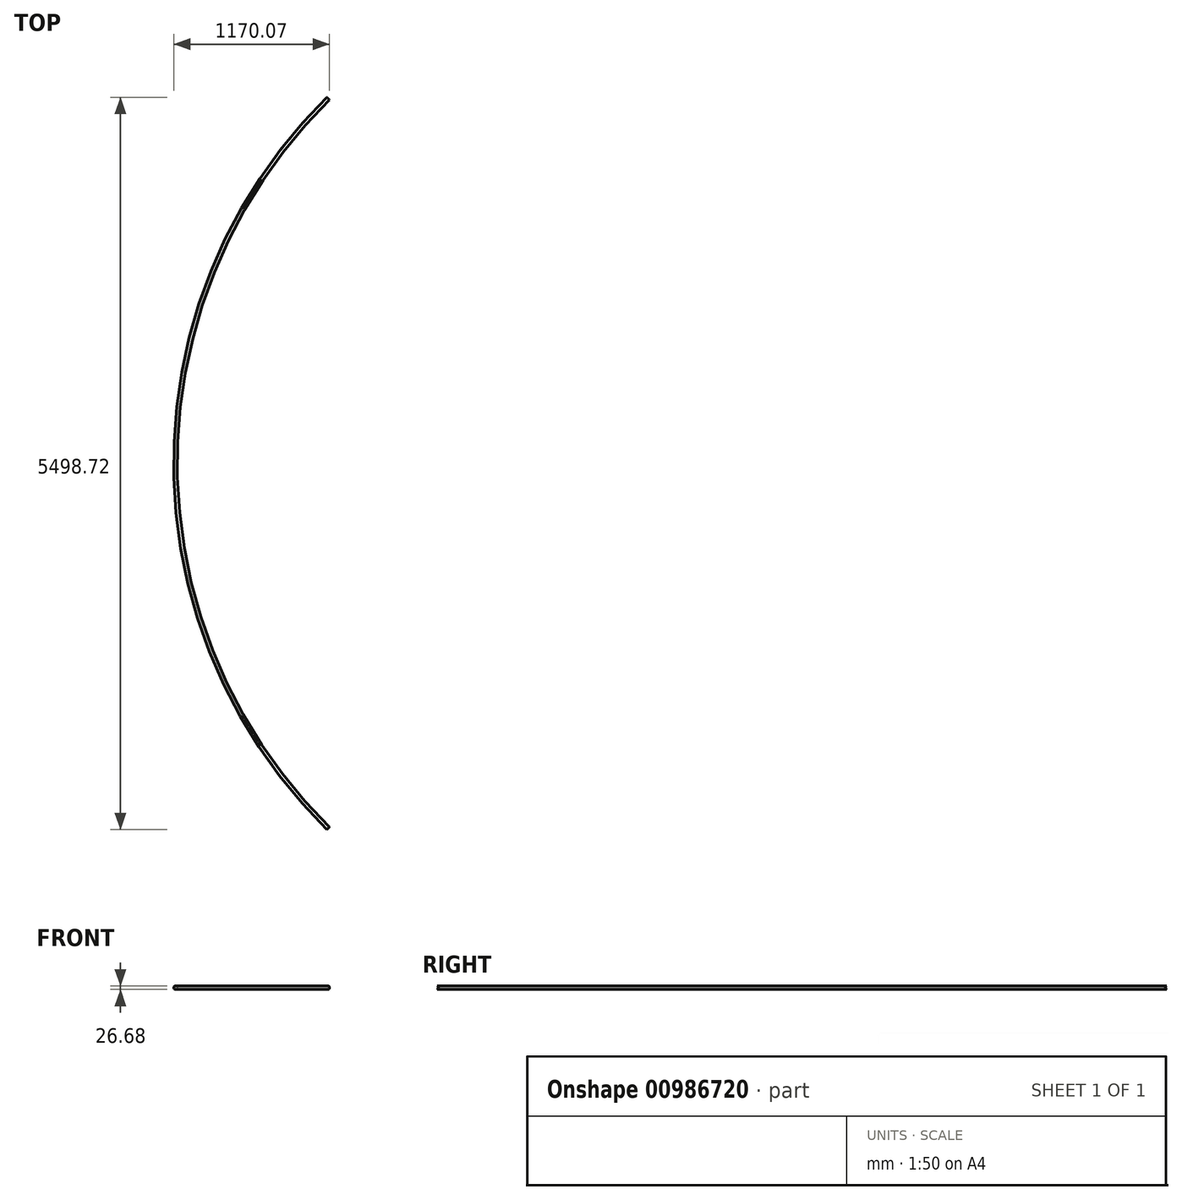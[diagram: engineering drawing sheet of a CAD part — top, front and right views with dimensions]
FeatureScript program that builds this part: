
annotation { "Feature Type Name" : "Feature", "Feature Type Description" : "" }
export const myFeature = defineFeature(function(context is Context, id is Id, definition is map)
    precondition{}
    {
        {
            var Q0;
            Q0=qCreatedBy(makeId("Front.planeOp"),FACE);
            var sketch = newSketch(context, id + "F0", { "sketchPlane" : qUnion([Q0])});
            skLineSegment(sketch, "E0", {"start": v(0, 0) * mm, "end": v(3845, 0) * mm, "construction": true});
            skLineSegment(sketch, "E1", {"start": v(3845, 0) * mm, "end": v(3845, -100) * mm, "construction": true});
            skCircle(sketch, "E2", {"center": v(0, 0) * mm, "radius": 13.34 * mm});
            skCircle(sketch, "E3.0", {"center": v(0, 0) * mm, "radius": 11.23 * mm});
            skSolve(sketch);
        }
        {
            var Q0;
            Q0=qSketchRegion(id+"F0",true);
            var Q1;
            Q1=sQuery(id+"F0.wireOp",EDGE,"E1");
            revolve(context, id + "F1", {"surfaceOperationType" : NewSurfaceOperationType.NEW, "entities" : qUnion([Q0]), "axis" : qUnion([Q1]), "revolveType" : RevolveType.SYMMETRIC, "angle" : 90.89 * degree});
        }
    });
